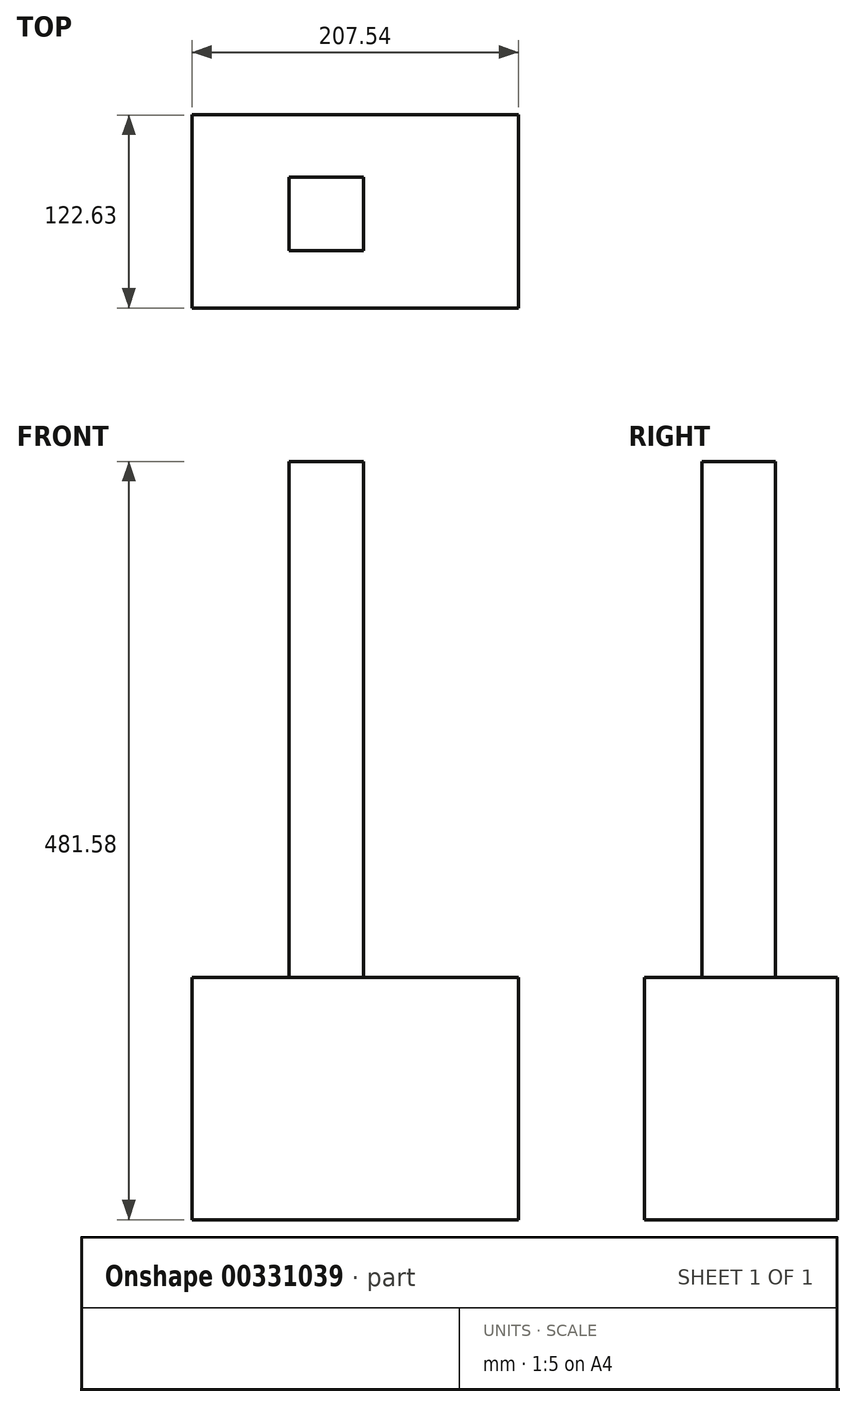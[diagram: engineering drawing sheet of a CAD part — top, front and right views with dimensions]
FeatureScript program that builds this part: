
annotation { "Feature Type Name" : "Feature", "Feature Type Description" : "" }
export const myFeature = defineFeature(function(context is Context, id is Id, definition is map)
    precondition{}
    {
        {
            var Q0;
            Q0=qCreatedBy(makeId("Top.planeOp"),FACE);
            var sketch = newSketch(context, id + "F0", { "sketchPlane" : qUnion([Q0])});
            skCircle(sketch, "E0", {"center": v(-377.32, 319.9) * mm, "radius": 63.5 * mm});
            skLineSegment(sketch, "E1.bottom", {"start": v(108.5, 232.64) * mm, "end": v(316.03, 232.64) * mm});
            skLineSegment(sketch, "E1.top", {"start": v(108.5, 110) * mm, "end": v(316.03, 110) * mm});
            skLineSegment(sketch, "E1.left", {"start": v(108.5, 232.64) * mm, "end": v(108.5, 110) * mm});
            skLineSegment(sketch, "E1.right", {"start": v(316.03, 232.64) * mm, "end": v(316.03, 110) * mm});
            skLineSegment(sketch, "E2", {"start": v(-335.96, -77.57) * mm, "end": v(-142.58, -143.6) * mm});
            skLineSegment(sketch, "E3", {"start": v(-142.58, -143.6) * mm, "end": v(-142.58, -336.98) * mm});
            skLineSegment(sketch, "E4", {"start": v(-142.58, -336.98) * mm, "end": v(-364.26, -372.36) * mm});
            skLineSegment(sketch, "E5", {"start": v(-364.26, -372.36) * mm, "end": v(-335.96, -77.57) * mm});
            skLineSegment(sketch, "E6", {"start": v(-277, -160.1) * mm, "end": v(-310.02, -292.17) * mm});
            skLineSegment(sketch, "E7", {"start": v(-310.02, -292.17) * mm, "end": v(-239, -309.93) * mm});
            skLineSegment(sketch, "E8", {"start": v(-239, -309.93) * mm, "end": v(-277, -160.1) * mm});
            skSolve(sketch);
        }
        {
            var Q0;
            Q0=makeQuery(id+"F0.imprint","IMPRINT",FACE,{"disambiguationData":[TD([[makeQuery(id+"F0.imprint","IMPRINT",EDGE,{"derivedFrom":sQuery(id+"F0.wireOp",EDGE,"E1.bottom")}),-1.0]])]});
            extrude(context, id + "F1", {"entities" : qUnion([Q0]), "depth" : 153.92 * mm, "offsetDistance" : 25.4 * mm});
        }
        {
            var Q0;
            Q0=makeQuery(id+"F1.opExtrude","CAP_FACE",FACE,{"disambiguationData":[OSD([sQuery(id+"F0.wireOp",EDGE,"E1.bottom"),sQuery(id+"F0.wireOp",EDGE,"E1.top"),sQuery(id+"F0.wireOp",EDGE,"E1.left"),sQuery(id+"F0.wireOp",EDGE,"E1.right")])],"isStart":false});
            var sketch = newSketch(context, id + "F2", { "sketchPlane" : qUnion([Q0])});
            skLineSegment(sketch, "E9.bottom", {"start": v(170.38, 193.03) * mm, "end": v(217.65, 193.03) * mm});
            skLineSegment(sketch, "E9.top", {"start": v(170.38, 146.45) * mm, "end": v(217.65, 146.45) * mm});
            skLineSegment(sketch, "E9.left", {"start": v(170.38, 193.03) * mm, "end": v(170.38, 146.45) * mm});
            skLineSegment(sketch, "E9.right", {"start": v(217.65, 193.03) * mm, "end": v(217.65, 146.45) * mm});
            skSolve(sketch);
        }
        {
            var Q0;
            Q0 = qSketchRegion(id + "F2", true);
            extrude(context, id + "F3", {"entities" : qUnion([Q0]), "depth" : 327.66 * mm, "offsetDistance" : 25.4 * mm});
        }
    });
